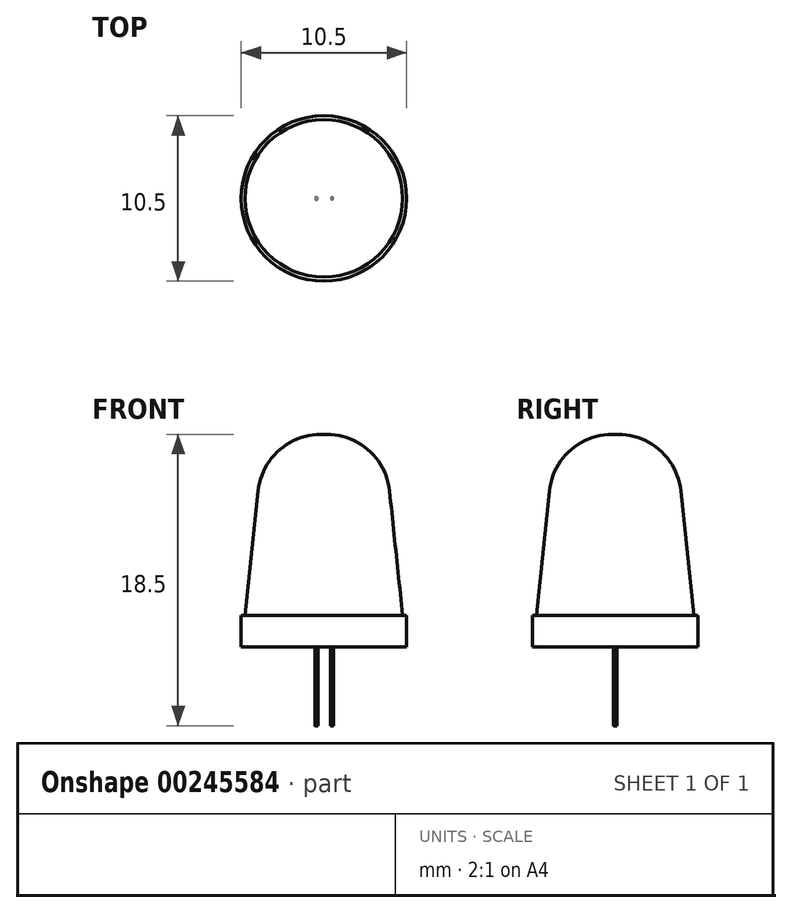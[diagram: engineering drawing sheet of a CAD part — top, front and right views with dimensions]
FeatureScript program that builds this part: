
annotation { "Feature Type Name" : "Feature", "Feature Type Description" : "" }
export const myFeature = defineFeature(function(context is Context, id is Id, definition is map)
    precondition{}
    {
        {
            var Q0;
            Q0=qCreatedBy(makeId("Front.planeOp"),FACE);
            var sketch = newSketch(context, id + "F0", { "sketchPlane" : qUnion([Q0])});
            skLineSegment(sketch, "E0", {"start": v(-5.25, 0) * mm, "end": v(-5.25, 2) * mm});
            skLineSegment(sketch, "E1", {"start": v(-5.25, 2) * mm, "end": v(-5, 2) * mm});
            skLineSegment(sketch, "E2", {"start": v(-5, 2) * mm, "end": v(-3.8, 13.5) * mm});
            skLineSegment(sketch, "E3", {"start": v(-3.8, 13.5) * mm, "end": v(0, 13.5) * mm});
            skLineSegment(sketch, "E4", {"start": v(0, 13.5) * mm, "end": v(0, 0) * mm});
            skLineSegment(sketch, "E5", {"start": v(0, 0) * mm, "end": v(-5.25, 0) * mm});
            skSolve(sketch);
        }
        {
            var Q0;
            Q0 = qSketchRegion(id + "F0", true);
            var Q1;
            Q1=sQuery(id+"F0.wireOp",EDGE,"E4");
            revolve(context, id + "F1", {"entities" : qUnion([Q0]), "axis" : qUnion([Q1]), "revolveType" : RevolveType.FULL});
        }
        {
            var Q0;
            Q0=makeQuery(id+"F1.opRevolve","SWEPT_EDGE",EDGE,{"disambiguationData":[OSD([sQuery(id+"F0.wireOp",EDGE,"E2"),sQuery(id+"F0.wireOp",EDGE,"E3")])]});
            fillet(context, id + "F2", {"entities" : qUnion([Q0]), "radius" : 4 * mm, "tangentPropagation" : true, "allowEdgeOverflow" : false});
        }
        {
            var Q0;
            Q0=makeQuery(id+"F1.opRevolve","SWEPT_FACE",FACE,{"disambiguationData":[OSD([sQuery(id+"F0.wireOp",EDGE,"E5")])]});
            var sketch = newSketch(context, id + "F3", { "sketchPlane" : qUnion([Q0])});
            skCircle(sketch, "E6", {"center": v(-0.48, 0) * mm, "radius": 0.1 * mm});
            skCircle(sketch, "E7", {"center": v(0.52, 0) * mm, "radius": 0.09 * mm});
            skSolve(sketch);
        }
        {
            var Q0;
            Q0 = qSketchRegion(id + "F3", true);
            extrude(context, id + "F4", {"entities" : qUnion([Q0]), "depth" : 5 * mm});
        }
    });
